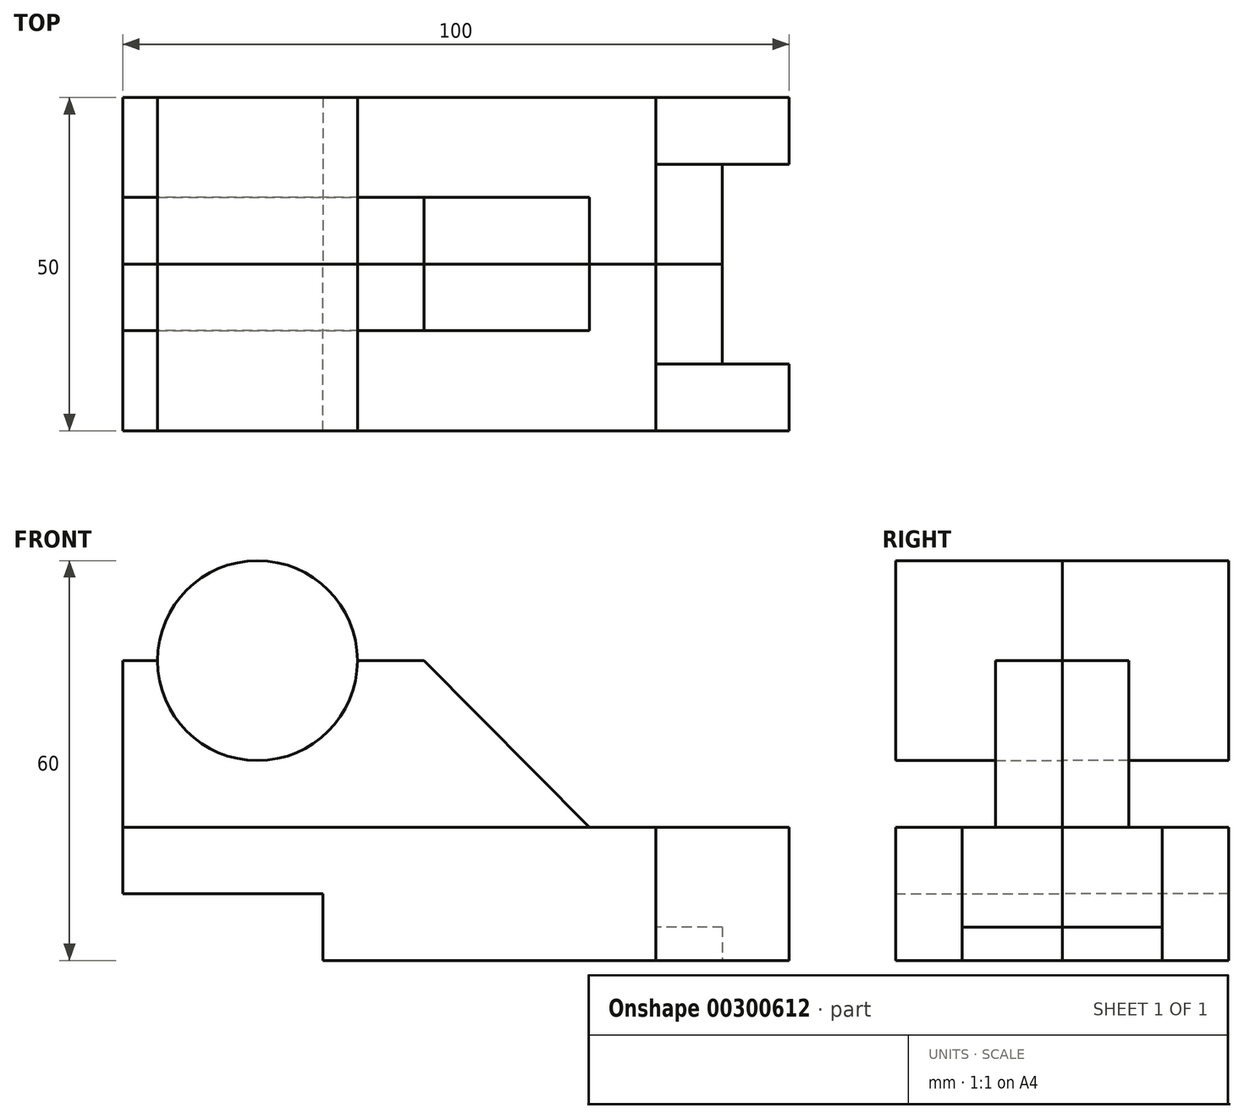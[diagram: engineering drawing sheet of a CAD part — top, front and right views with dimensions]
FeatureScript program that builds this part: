
annotation { "Feature Type Name" : "Feature", "Feature Type Description" : "" }
export const myFeature = defineFeature(function(context is Context, id is Id, definition is map)
    precondition{}
    {
        {
            var Q0;
            Q0=qCreatedBy(makeId("Front.planeOp"),FACE);
            var sketch = newSketch(context, id + "F0", { "sketchPlane" : qUnion([Q0])});
            skLineSegment(sketch, "E0", {"start": v(20.28, 21.26) * mm, "end": v(-29.72, 21.26) * mm});
            skLineSegment(sketch, "E1", {"start": v(-29.72, 21.26) * mm, "end": v(-29.72, 31.26) * mm});
            skLineSegment(sketch, "E2", {"start": v(-29.72, 31.26) * mm, "end": v(-59.72, 31.26) * mm});
            skLineSegment(sketch, "E3", {"start": v(-59.72, 31.26) * mm, "end": v(-59.72, 41.26) * mm});
            skLineSegment(sketch, "E4", {"start": v(20.28, 41.26) * mm, "end": v(20.28, 21.26) * mm});
            skLineSegment(sketch, "E5", {"start": v(20.28, 41.26) * mm, "end": v(10.28, 41.26) * mm});
            skLineSegment(sketch, "E6", {"start": v(10.28, 41.26) * mm, "end": v(-59.72, 41.26) * mm});
            skLineSegment(sketch, "E7", {"start": v(10.28, 41.26) * mm, "end": v(-14.5, 66.26) * mm});
            skLineSegment(sketch, "E8", {"start": v(-14.5, 66.26) * mm, "end": v(-24.5, 66.26) * mm});
            skCircle(sketch, "E9", {"center": v(-39.5, 66.26) * mm, "radius": 15 * mm});
            skPoint(sketch, "E9.first.point", {"position": v(-54.5, 66.26) * mm});
            skPoint(sketch, "E9.third.point", {"position": v(-38.64, 51.29) * mm});
            skLineSegment(sketch, "E10", {"start": v(-54.5, 66.26) * mm, "end": v(-59.72, 66.26) * mm});
            skLineSegment(sketch, "E11", {"start": v(-59.72, 66.26) * mm, "end": v(-59.72, 41.26) * mm});
            skSolve(sketch);
        }
        {
            var Q0;
            {var subQ0=sQuery(id+"F0.wireOp",EDGE,"E9");var subQ1=makeQuery(id+"F0.imprint","INTERSECT",VERTEX,{"derivedFrom":[sQuery(id+"F0.wireOp",EDGE,"E8"),subQ0]});Q0=makeQuery(id+"F0.imprint","IMPRINT",FACE,{"disambiguationData":[TD([[makeQuery(id+"F0.imprint","IMPRINT",EDGE,{"disambiguationData":[TD([[subQ1,-1.0]])],"derivedFrom":subQ0}),1.0]])]});}
            var Q1;
            Q1=makeQuery(id+"F0.imprint","IMPRINT",FACE,{"disambiguationData":[TD([[makeQuery(id+"F0.imprint","IMPRINT",EDGE,{"derivedFrom":sQuery(id+"F0.wireOp",EDGE,"E0")}),-1.0]])]});
            extrude(context, id + "F1", {"entities" : qUnion([Q0, Q1]), "depth" : 25 * mm});
        }
        {
            var Q0;
            Q0=makeQuery(id+"F1.opExtrude","CAP_FACE",FACE,{"disambiguationData":[OSD([sQuery(id+"F0.wireOp",EDGE,"E9")])],"isStart":true});
            var Q1;
            Q1=makeQuery(id+"F1.opExtrude","CAP_FACE",FACE,{"disambiguationData":[OSD([sQuery(id+"F0.wireOp",EDGE,"E0"),sQuery(id+"F0.wireOp",EDGE,"E1"),sQuery(id+"F0.wireOp",EDGE,"E2"),sQuery(id+"F0.wireOp",EDGE,"E3"),sQuery(id+"F0.wireOp",EDGE,"E4"),sQuery(id+"F0.wireOp",EDGE,"E5"),sQuery(id+"F0.wireOp",EDGE,"E6")])],"isStart":true});
            extrude(context, id + "F2", {"entities" : qUnion([Q0, Q1]), "depth" : 25 * mm});
        }
        {
            var Q0;
            Q0=makeQuery(id+"F0.imprint","IMPRINT",FACE,{"disambiguationData":[TD([[makeQuery(id+"F0.imprint","IMPRINT",EDGE,{"derivedFrom":sQuery(id+"F0.wireOp",EDGE,"E6")}),-1.0]])]});
            extrude(context, id + "F3", {"entities" : qUnion([Q0]), "depth" : 10 * mm});
        }
        {
            var Q0;
            Q0=makeQuery(id+"F0.imprint","IMPRINT",FACE,{"disambiguationData":[TD([[makeQuery(id+"F0.imprint","IMPRINT",EDGE,{"derivedFrom":sQuery(id+"F0.wireOp",EDGE,"E6")}),-1.0]])]});
            extrude(context, id + "F4", {"entities" : qUnion([Q0]), "oppositeDirection" : true, "depth" : 10 * mm});
        }
        {
            var Q0;
            Q0=makeQuery(id+"F1.opExtrude","SWEPT_FACE",FACE,{"disambiguationData":[OSD([sQuery(id+"F0.wireOp",EDGE,"E4")])]});
            var sketch = newSketch(context, id + "F5", { "sketchPlane" : qUnion([Q0])});
            skLineSegment(sketch, "E12", {"start": v(-15, 41.26) * mm, "end": v(-15, 21.26) * mm});
            skLineSegment(sketch, "E13", {"start": v(-15, 26.26) * mm, "end": v(0, 26.26) * mm});
            skSolve(sketch);
        }
        {
            var Q0;
            Q0=makeQuery(id+"F2.opExtrude","SWEPT_FACE",FACE,{"disambiguationData":[OSD([sQuery(id+"F0.wireOp",EDGE,"E4")])]});
            var sketch = newSketch(context, id + "F6", { "sketchPlane" : qUnion([Q0])});
            skLineSegment(sketch, "E14", {"start": v(15, 41.26) * mm, "end": v(15, 21.26) * mm});
            skLineSegment(sketch, "E15", {"start": v(0, 26.26) * mm, "end": v(15, 26.26) * mm});
            skSolve(sketch);
        }
        {
            var Q0;
            {var subQ0=sQuery(id+"F5.wireOp",EDGE,"E12");Q0=makeQuery(id+"F5.imprint","IMPRINT",FACE,{"disambiguationData":[TD([[makeQuery(id+"F5.imprint","IMPRINT",EDGE,{"derivedFrom":subQ0}),-1.0]])]});}
            var Q1;
            {var subQ0=sQuery(id+"F6.wireOp",EDGE,"E14");Q1=makeQuery(id+"F6.imprint","IMPRINT",FACE,{"disambiguationData":[TD([[makeQuery(id+"F6.imprint","IMPRINT",EDGE,{"derivedFrom":subQ0}),1.0]])]});}
            extrude(context, id + "F7", {"entities" : qUnion([Q0, Q1]), "depth" : 20 * mm});
        }
        {
            var Q0;
            {var subQ4=sQuery(id+"F5.wireOp",EDGE,"E13");Q0=makeQuery(id+"F5.imprint","IMPRINT",FACE,{"disambiguationData":[TD([[makeQuery(id+"F5.imprint","IMPRINT",EDGE,{"derivedFrom":subQ4}),-1.0]])]});}
            var Q1;
            {var subQ4=sQuery(id+"F6.wireOp",EDGE,"E15");Q1=makeQuery(id+"F6.imprint","IMPRINT",FACE,{"disambiguationData":[TD([[makeQuery(id+"F6.imprint","IMPRINT",EDGE,{"derivedFrom":subQ4}),-1.0]])]});}
            extrude(context, id + "F8", {"entities" : qUnion([Q0, Q1]), "depth" : 10 * mm});
        }
    });
